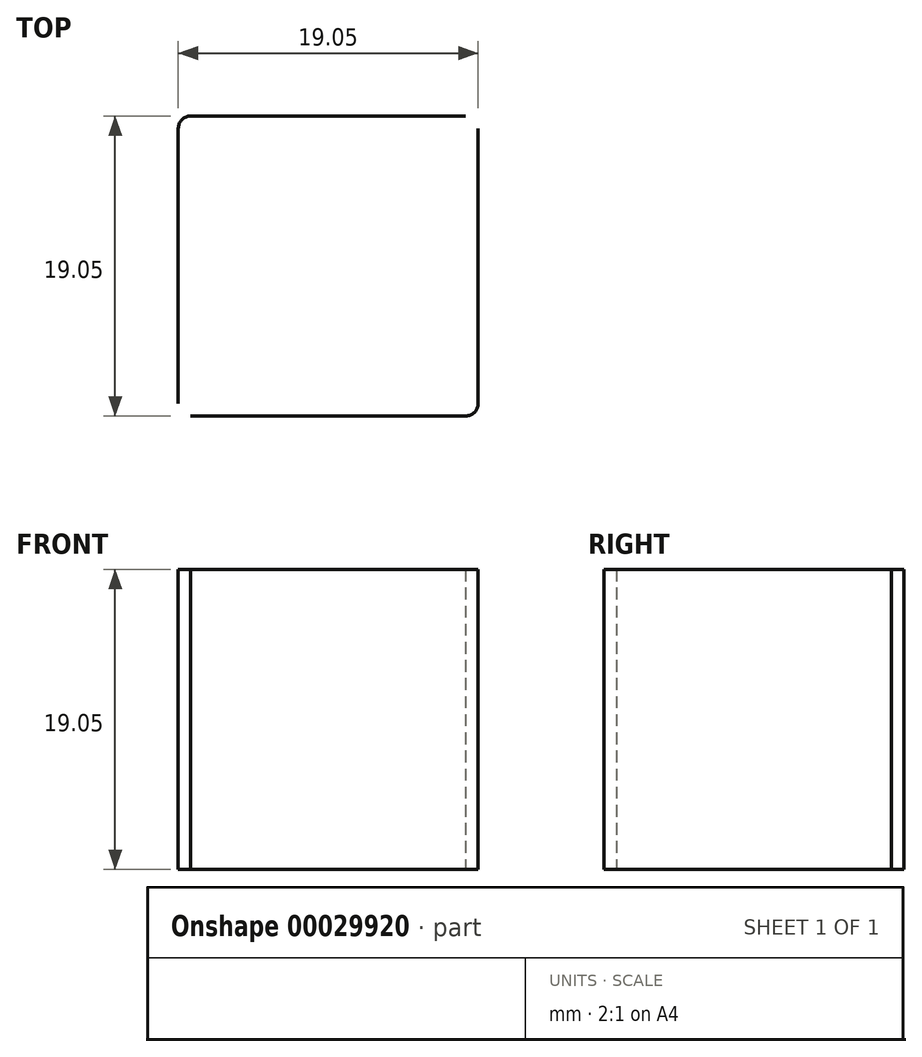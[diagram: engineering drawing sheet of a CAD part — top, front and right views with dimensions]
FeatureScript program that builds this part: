
annotation { "Feature Type Name" : "Feature", "Feature Type Description" : "" }
export const myFeature = defineFeature(function(context is Context, id is Id, definition is map)
    precondition{}
    {
        {
            var Q0;
            Q0=qCreatedBy(makeId("Top.planeOp"),FACE);
            var sketch = newSketch(context, id + "F0", { "sketchPlane" : qUnion([Q0])});
            skLineSegment(sketch, "E0.bottom", {"start": v(-34.1, 33.67) * mm, "end": v(-16.64, 33.67) * mm});
            skLineSegment(sketch, "E0.top", {"start": v(-34.1, -23.48) * mm, "end": v(-16.64, -23.48) * mm});
            skLineSegment(sketch, "E0.left", {"start": v(-34.9, 32.88) * mm, "end": v(-34.9, 15.42) * mm});
            skLineSegment(sketch, "E0.right", {"start": v(22.25, 32.88) * mm, "end": v(22.25, 15.42) * mm});
            skLineSegment(sketch, "E1", {"start": v(-34.9, -22.68) * mm, "end": v(-34.9, -5.22) * mm});
            skLineSegment(sketch, "E2", {"start": v(-34.1, -4.43) * mm, "end": v(-16.64, -4.43) * mm});
            skLineSegment(sketch, "E3", {"start": v(-15.85, -22.68) * mm, "end": v(-15.85, -5.22) * mm});
            skLineSegment(sketch, "E4.0", {"start": v(-34.1, 14.62) * mm, "end": v(-16.64, 14.62) * mm});
            skLineSegment(sketch, "E5.0", {"start": v(3.2, -22.68) * mm, "end": v(3.2, -5.22) * mm});
            skLineSegment(sketch, "E6.bottom", {"start": v(-33.23, -5.2) * mm, "end": v(-17.36, -5.2) * mm});
            skLineSegment(sketch, "E6.top", {"start": v(-33.23, -22.66) * mm, "end": v(-17.36, -22.66) * mm});
            skLineSegment(sketch, "E6.left", {"start": v(-34.03, -6) * mm, "end": v(-34.03, -21.87) * mm});
            skLineSegment(sketch, "E6.right", {"start": v(-16.56, -6) * mm, "end": v(-16.56, -21.87) * mm});
            skPoint(sketch, "E7.visualSharp", {"position": v(-34.03, -5.2) * mm});
            skArc(sketch, "E7.filletArc", {"start": v(-33.23, -5.2) * mm, "mid": v(-33.8, -5.43) * mm, "end": v(-34.03, -6) * mm});
            skPoint(sketch, "E8.visualSharp", {"position": v(-16.56, -5.2) * mm});
            skArc(sketch, "E8.filletArc", {"start": v(-16.56, -6) * mm, "mid": v(-16.8, -5.43) * mm, "end": v(-17.36, -5.2) * mm});
            skPoint(sketch, "E9.visualSharp", {"position": v(-16.56, -22.66) * mm});
            skArc(sketch, "E9.filletArc", {"start": v(-17.36, -22.66) * mm, "mid": v(-16.8, -22.43) * mm, "end": v(-16.56, -21.87) * mm});
            skPoint(sketch, "E10.visualSharp", {"position": v(-34.03, -22.66) * mm});
            skArc(sketch, "E10.filletArc", {"start": v(-34.03, -21.87) * mm, "mid": v(-33.8, -22.43) * mm, "end": v(-33.23, -22.66) * mm});
            skLineSegment(sketch, "E11.0.1.0", {"start": v(-34.03, 13.06) * mm, "end": v(-34.03, -2.82) * mm});
            skArc(sketch, "E11.0.1.1", {"start": v(-34.03, -2.82) * mm, "mid": v(-33.8, -3.38) * mm, "end": v(-33.23, -3.61) * mm});
            skLineSegment(sketch, "E11.0.1.2", {"start": v(-33.23, -3.61) * mm, "end": v(-17.36, -3.61) * mm});
            skArc(sketch, "E11.0.1.3", {"start": v(-17.36, -3.61) * mm, "mid": v(-16.8, -3.38) * mm, "end": v(-16.56, -2.82) * mm});
            skLineSegment(sketch, "E11.0.1.4", {"start": v(-16.56, 13.06) * mm, "end": v(-16.56, -2.82) * mm});
            skArc(sketch, "E11.0.1.5", {"start": v(-16.56, 13.06) * mm, "mid": v(-16.8, 13.62) * mm, "end": v(-17.36, 13.85) * mm});
            skLineSegment(sketch, "E11.0.1.6", {"start": v(-33.23, 13.85) * mm, "end": v(-17.36, 13.85) * mm});
            skArc(sketch, "E11.0.1.7", {"start": v(-33.23, 13.85) * mm, "mid": v(-33.8, 13.62) * mm, "end": v(-34.03, 13.06) * mm});
            skLineSegment(sketch, "E11.0.2.0", {"start": v(-34.03, 32.1) * mm, "end": v(-34.03, 16.23) * mm});
            skArc(sketch, "E11.0.2.1", {"start": v(-34.03, 16.23) * mm, "mid": v(-33.8, 15.67) * mm, "end": v(-33.23, 15.44) * mm});
            skLineSegment(sketch, "E11.0.2.2", {"start": v(-33.23, 15.44) * mm, "end": v(-17.36, 15.44) * mm});
            skArc(sketch, "E11.0.2.3", {"start": v(-17.36, 15.44) * mm, "mid": v(-16.8, 15.67) * mm, "end": v(-16.56, 16.23) * mm});
            skLineSegment(sketch, "E11.0.2.4", {"start": v(-16.56, 32.1) * mm, "end": v(-16.56, 16.23) * mm});
            skArc(sketch, "E11.0.2.5", {"start": v(-16.56, 32.1) * mm, "mid": v(-16.8, 32.67) * mm, "end": v(-17.36, 32.9) * mm});
            skLineSegment(sketch, "E11.0.2.6", {"start": v(-33.23, 32.9) * mm, "end": v(-17.36, 32.9) * mm});
            skArc(sketch, "E11.0.2.7", {"start": v(-33.23, 32.9) * mm, "mid": v(-33.8, 32.67) * mm, "end": v(-34.03, 32.1) * mm});
            skLineSegment(sketch, "E11.1.0.0", {"start": v(-14.98, -6) * mm, "end": v(-14.98, -21.87) * mm});
            skArc(sketch, "E11.1.0.1", {"start": v(-14.98, -21.87) * mm, "mid": v(-14.74, -22.43) * mm, "end": v(-14.18, -22.66) * mm});
            skLineSegment(sketch, "E11.1.0.2", {"start": v(-14.18, -22.66) * mm, "end": v(1.7, -22.66) * mm});
            skArc(sketch, "E11.1.0.3", {"start": v(1.7, -22.66) * mm, "mid": v(2.25, -22.43) * mm, "end": v(2.49, -21.87) * mm});
            skLineSegment(sketch, "E11.1.0.4", {"start": v(2.49, -6) * mm, "end": v(2.49, -21.87) * mm});
            skArc(sketch, "E11.1.0.5", {"start": v(2.49, -6) * mm, "mid": v(2.25, -5.43) * mm, "end": v(1.7, -5.2) * mm});
            skLineSegment(sketch, "E11.1.0.6", {"start": v(-14.18, -5.2) * mm, "end": v(1.7, -5.2) * mm});
            skArc(sketch, "E11.1.0.7", {"start": v(-14.18, -5.2) * mm, "mid": v(-14.74, -5.43) * mm, "end": v(-14.98, -6) * mm});
            skLineSegment(sketch, "E11.1.1.0", {"start": v(-14.98, 13.06) * mm, "end": v(-14.98, -2.82) * mm});
            skArc(sketch, "E11.1.1.1", {"start": v(-14.98, -2.82) * mm, "mid": v(-14.74, -3.38) * mm, "end": v(-14.18, -3.61) * mm});
            skLineSegment(sketch, "E11.1.1.2", {"start": v(-14.18, -3.61) * mm, "end": v(1.7, -3.61) * mm});
            skArc(sketch, "E11.1.1.3", {"start": v(1.7, -3.61) * mm, "mid": v(2.25, -3.38) * mm, "end": v(2.49, -2.82) * mm});
            skLineSegment(sketch, "E11.1.1.4", {"start": v(2.49, 13.06) * mm, "end": v(2.49, -2.82) * mm});
            skArc(sketch, "E11.1.1.5", {"start": v(2.49, 13.06) * mm, "mid": v(2.25, 13.62) * mm, "end": v(1.7, 13.85) * mm});
            skLineSegment(sketch, "E11.1.1.6", {"start": v(-14.18, 13.85) * mm, "end": v(1.7, 13.85) * mm});
            skArc(sketch, "E11.1.1.7", {"start": v(-14.18, 13.85) * mm, "mid": v(-14.74, 13.62) * mm, "end": v(-14.98, 13.06) * mm});
            skLineSegment(sketch, "E11.1.2.0", {"start": v(-14.98, 32.1) * mm, "end": v(-14.98, 16.23) * mm});
            skArc(sketch, "E11.1.2.1", {"start": v(-14.98, 16.23) * mm, "mid": v(-14.74, 15.67) * mm, "end": v(-14.18, 15.44) * mm});
            skLineSegment(sketch, "E11.1.2.2", {"start": v(-14.18, 15.44) * mm, "end": v(1.7, 15.44) * mm});
            skArc(sketch, "E11.1.2.3", {"start": v(1.7, 15.44) * mm, "mid": v(2.25, 15.67) * mm, "end": v(2.49, 16.23) * mm});
            skLineSegment(sketch, "E11.1.2.4", {"start": v(2.49, 32.1) * mm, "end": v(2.49, 16.23) * mm});
            skArc(sketch, "E11.1.2.5", {"start": v(2.49, 32.1) * mm, "mid": v(2.25, 32.67) * mm, "end": v(1.7, 32.9) * mm});
            skLineSegment(sketch, "E11.1.2.6", {"start": v(-14.18, 32.9) * mm, "end": v(1.7, 32.9) * mm});
            skArc(sketch, "E11.1.2.7", {"start": v(-14.18, 32.9) * mm, "mid": v(-14.74, 32.67) * mm, "end": v(-14.98, 32.1) * mm});
            skLineSegment(sketch, "E11.2.0.0", {"start": v(4.07, -6) * mm, "end": v(4.07, -21.87) * mm});
            skArc(sketch, "E11.2.0.1", {"start": v(4.07, -21.87) * mm, "mid": v(4.3, -22.43) * mm, "end": v(4.87, -22.66) * mm});
            skLineSegment(sketch, "E11.2.0.2", {"start": v(4.87, -22.66) * mm, "end": v(20.74, -22.66) * mm});
            skArc(sketch, "E11.2.0.3", {"start": v(20.74, -22.66) * mm, "mid": v(21.3, -22.43) * mm, "end": v(21.54, -21.87) * mm});
            skLineSegment(sketch, "E11.2.0.4", {"start": v(21.54, -6) * mm, "end": v(21.54, -21.87) * mm});
            skArc(sketch, "E11.2.0.5", {"start": v(21.54, -6) * mm, "mid": v(21.3, -5.43) * mm, "end": v(20.74, -5.2) * mm});
            skLineSegment(sketch, "E11.2.0.6", {"start": v(4.87, -5.2) * mm, "end": v(20.74, -5.2) * mm});
            skArc(sketch, "E11.2.0.7", {"start": v(4.87, -5.2) * mm, "mid": v(4.3, -5.43) * mm, "end": v(4.07, -6) * mm});
            skLineSegment(sketch, "E11.2.1.0", {"start": v(4.07, 13.06) * mm, "end": v(4.07, -2.82) * mm});
            skArc(sketch, "E11.2.1.1", {"start": v(4.07, -2.82) * mm, "mid": v(4.3, -3.38) * mm, "end": v(4.87, -3.61) * mm});
            skLineSegment(sketch, "E11.2.1.2", {"start": v(4.87, -3.61) * mm, "end": v(20.74, -3.61) * mm});
            skArc(sketch, "E11.2.1.3", {"start": v(20.74, -3.61) * mm, "mid": v(21.3, -3.38) * mm, "end": v(21.54, -2.82) * mm});
            skLineSegment(sketch, "E11.2.1.4", {"start": v(21.54, 13.06) * mm, "end": v(21.54, -2.82) * mm});
            skArc(sketch, "E11.2.1.5", {"start": v(21.54, 13.06) * mm, "mid": v(21.3, 13.62) * mm, "end": v(20.74, 13.85) * mm});
            skLineSegment(sketch, "E11.2.1.6", {"start": v(4.87, 13.85) * mm, "end": v(20.74, 13.85) * mm});
            skArc(sketch, "E11.2.1.7", {"start": v(4.87, 13.85) * mm, "mid": v(4.3, 13.62) * mm, "end": v(4.07, 13.06) * mm});
            skLineSegment(sketch, "E11.2.2.0", {"start": v(4.07, 32.1) * mm, "end": v(4.07, 16.23) * mm});
            skArc(sketch, "E11.2.2.1", {"start": v(4.07, 16.23) * mm, "mid": v(4.3, 15.67) * mm, "end": v(4.87, 15.44) * mm});
            skLineSegment(sketch, "E11.2.2.2", {"start": v(4.87, 15.44) * mm, "end": v(20.74, 15.44) * mm});
            skArc(sketch, "E11.2.2.3", {"start": v(20.74, 15.44) * mm, "mid": v(21.3, 15.67) * mm, "end": v(21.54, 16.23) * mm});
            skLineSegment(sketch, "E11.2.2.4", {"start": v(21.54, 32.1) * mm, "end": v(21.54, 16.23) * mm});
            skArc(sketch, "E11.2.2.5", {"start": v(21.54, 32.1) * mm, "mid": v(21.3, 32.67) * mm, "end": v(20.74, 32.9) * mm});
            skLineSegment(sketch, "E11.2.2.6", {"start": v(4.87, 32.9) * mm, "end": v(20.74, 32.9) * mm});
            skArc(sketch, "E11.2.2.7", {"start": v(4.87, 32.9) * mm, "mid": v(4.3, 32.67) * mm, "end": v(4.07, 32.1) * mm});
            skLineSegment(sketch, "E12", {"start": v(3.2, 15.42) * mm, "end": v(3.2, 32.88) * mm});
            skLineSegment(sketch, "E13", {"start": v(3.2, -3.63) * mm, "end": v(3.2, 13.83) * mm});
            skLineSegment(sketch, "E14", {"start": v(4, -4.43) * mm, "end": v(21.46, -4.43) * mm});
            skLineSegment(sketch, "E15", {"start": v(4, 14.62) * mm, "end": v(21.46, 14.62) * mm});
            skLineSegment(sketch, "E16", {"start": v(-15.05, 14.62) * mm, "end": v(2.41, 14.62) * mm});
            skLineSegment(sketch, "E17", {"start": v(-15.05, -4.43) * mm, "end": v(2.41, -4.43) * mm});
            skLineSegment(sketch, "E18", {"start": v(-15.85, -3.63) * mm, "end": v(-15.85, 13.83) * mm});
            skLineSegment(sketch, "E19", {"start": v(-15.85, 15.42) * mm, "end": v(-15.85, 32.88) * mm});
            skLineSegment(sketch, "E20", {"start": v(22.25, 13.83) * mm, "end": v(22.25, -3.63) * mm});
            skLineSegment(sketch, "E21", {"start": v(22.25, -5.22) * mm, "end": v(22.25, -22.68) * mm});
            skLineSegment(sketch, "E22", {"start": v(4, -23.48) * mm, "end": v(21.46, -23.48) * mm});
            skLineSegment(sketch, "E23", {"start": v(-15.05, -23.48) * mm, "end": v(2.41, -23.48) * mm});
            skLineSegment(sketch, "E24", {"start": v(-34.9, -5.22) * mm, "end": v(-34.9, -22.68) * mm});
            skLineSegment(sketch, "E25", {"start": v(-34.9, 13.83) * mm, "end": v(-34.9, -3.63) * mm});
            skLineSegment(sketch, "E26", {"start": v(4, 33.67) * mm, "end": v(21.46, 33.67) * mm});
            skLineSegment(sketch, "E27", {"start": v(-15.05, 33.67) * mm, "end": v(2.41, 33.67) * mm});
            skArc(sketch, "E28.filletArc", {"start": v(3.2, 15.42) * mm, "mid": v(3.44, 14.86) * mm, "end": v(4, 14.62) * mm});
            skArc(sketch, "E29.filletArc", {"start": v(21.46, 14.62) * mm, "mid": v(22.02, 14.86) * mm, "end": v(22.25, 15.42) * mm});
            skArc(sketch, "E30.filletArc", {"start": v(4, 33.67) * mm, "mid": v(3.44, 33.44) * mm, "end": v(3.2, 32.88) * mm});
            skArc(sketch, "E31.filletArc", {"start": v(22.25, 32.88) * mm, "mid": v(22.02, 33.44) * mm, "end": v(21.46, 33.67) * mm});
            skArc(sketch, "E32.filletArc", {"start": v(21.46, -4.43) * mm, "mid": v(22.02, -4.2) * mm, "end": v(22.25, -3.63) * mm});
            skArc(sketch, "E33.filletArc", {"start": v(3.2, -3.63) * mm, "mid": v(3.44, -4.2) * mm, "end": v(4, -4.43) * mm});
            skArc(sketch, "E34.filletArc", {"start": v(21.46, -23.48) * mm, "mid": v(22.02, -23.24) * mm, "end": v(22.25, -22.68) * mm});
            skArc(sketch, "E35.filletArc", {"start": v(3.2, -22.68) * mm, "mid": v(3.44, -23.24) * mm, "end": v(4, -23.48) * mm});
            skArc(sketch, "E36.filletArc", {"start": v(-34.1, 33.67) * mm, "mid": v(-34.66, 33.44) * mm, "end": v(-34.9, 32.88) * mm});
            skArc(sketch, "E37.filletArc", {"start": v(-15.85, 32.88) * mm, "mid": v(-16.08, 33.44) * mm, "end": v(-16.64, 33.67) * mm});
            skArc(sketch, "E38.filletArc", {"start": v(-15.05, 14.62) * mm, "mid": v(-15.61, 14.4) * mm, "end": v(-15.85, 13.83) * mm});
            skArc(sketch, "E39.filletArc", {"start": v(-16.64, 14.62) * mm, "mid": v(-16.08, 14.86) * mm, "end": v(-15.85, 15.42) * mm});
            skArc(sketch, "E40.filletArc", {"start": v(-34.9, 15.42) * mm, "mid": v(-34.66, 14.86) * mm, "end": v(-34.1, 14.62) * mm});
            skArc(sketch, "E41.filletArc", {"start": v(-15.85, -5.22) * mm, "mid": v(-16.08, -4.66) * mm, "end": v(-16.64, -4.43) * mm});
            skArc(sketch, "E42.filletArc", {"start": v(-15.85, -3.63) * mm, "mid": v(-15.61, -4.2) * mm, "end": v(-15.05, -4.43) * mm});
            skArc(sketch, "E43.filletArc", {"start": v(-15.85, -22.68) * mm, "mid": v(-15.61, -23.24) * mm, "end": v(-15.05, -23.48) * mm});
            skArc(sketch, "E44.filletArc", {"start": v(-34.1, -4.43) * mm, "mid": v(-34.66, -4.66) * mm, "end": v(-34.9, -5.22) * mm});
            skArc(sketch, "E45.filletArc", {"start": v(-34.9, -22.68) * mm, "mid": v(-34.66, -23.24) * mm, "end": v(-34.1, -23.48) * mm});
            skArc(sketch, "E46.filletArc", {"start": v(22.25, 13.83) * mm, "mid": v(22.02, 14.4) * mm, "end": v(21.46, 14.62) * mm});
            skArc(sketch, "E47.filletArc", {"start": v(4, 14.62) * mm, "mid": v(3.44, 14.4) * mm, "end": v(3.2, 13.83) * mm});
            skLineSegment(sketch, "E48", {"start": v(3.2, 13.83) * mm, "end": v(3.2, -3.63) * mm});
            skArc(sketch, "E49.filletArc", {"start": v(2.41, -4.43) * mm, "mid": v(2.97, -4.2) * mm, "end": v(3.2, -3.63) * mm});
            skArc(sketch, "E50.filletArc", {"start": v(-15.05, -4.43) * mm, "mid": v(-15.61, -4.66) * mm, "end": v(-15.85, -5.22) * mm});
            skArc(sketch, "E51.filletArc", {"start": v(-16.64, -23.48) * mm, "mid": v(-16.08, -23.24) * mm, "end": v(-15.85, -22.68) * mm});
            skLineSegment(sketch, "E52", {"start": v(-15.85, 13.83) * mm, "end": v(-15.85, -3.63) * mm});
            skLineSegment(sketch, "E53", {"start": v(-16.64, -4.43) * mm, "end": v(-34.1, -4.43) * mm});
            skLineSegment(sketch, "E54", {"start": v(-15.85, 32.88) * mm, "end": v(-15.85, 15.42) * mm});
            skArc(sketch, "E55.filletArc", {"start": v(-16.64, -4.43) * mm, "mid": v(-16.08, -4.2) * mm, "end": v(-15.85, -3.63) * mm});
            skArc(sketch, "E56.filletArc", {"start": v(3.2, -5.22) * mm, "mid": v(2.97, -4.66) * mm, "end": v(2.41, -4.43) * mm});
            skArc(sketch, "E57.filletArc", {"start": v(2.41, -23.48) * mm, "mid": v(2.97, -23.24) * mm, "end": v(3.2, -22.68) * mm});
            skArc(sketch, "E58.filletArc", {"start": v(-15.85, 13.83) * mm, "mid": v(-16.08, 14.4) * mm, "end": v(-16.64, 14.62) * mm});
            skArc(sketch, "E59.filletArc", {"start": v(-15.85, 15.42) * mm, "mid": v(-15.61, 14.86) * mm, "end": v(-15.05, 14.62) * mm});
            skArc(sketch, "E60.filletArc", {"start": v(-34.1, 14.62) * mm, "mid": v(-34.66, 14.4) * mm, "end": v(-34.9, 13.83) * mm});
            skArc(sketch, "E61.filletArc", {"start": v(3.2, 13.83) * mm, "mid": v(2.97, 14.4) * mm, "end": v(2.41, 14.62) * mm});
            skArc(sketch, "E62.filletArc", {"start": v(2.41, 14.62) * mm, "mid": v(2.97, 14.86) * mm, "end": v(3.2, 15.42) * mm});
            skArc(sketch, "E63.filletArc", {"start": v(-15.05, 33.67) * mm, "mid": v(-15.61, 33.44) * mm, "end": v(-15.85, 32.88) * mm});
            skArc(sketch, "E64.filletArc", {"start": v(3.2, 32.88) * mm, "mid": v(2.97, 33.44) * mm, "end": v(2.41, 33.67) * mm});
            skArc(sketch, "E65.filletArc", {"start": v(22.25, -5.22) * mm, "mid": v(22.02, -4.66) * mm, "end": v(21.46, -4.43) * mm});
            skArc(sketch, "E66.filletArc", {"start": v(-34.9, -3.63) * mm, "mid": v(-34.66, -4.2) * mm, "end": v(-34.1, -4.43) * mm});
            skArc(sketch, "E67.filletArc", {"start": v(4, -4.43) * mm, "mid": v(3.44, -4.66) * mm, "end": v(3.2, -5.22) * mm});
            skSolve(sketch);
        }
        {
            var Q0;
            Q0=sQuery(id+"F0.wireOp",EDGE,"E26");
            var Q1;
            Q1=sQuery(id+"F0.wireOp",EDGE,"E30.filletArc");
            var Q2;
            Q2=sQuery(id+"F0.wireOp",EDGE,"E12");
            var Q3;
            Q3=sQuery(id+"F0.wireOp",EDGE,"E29.filletArc");
            var Q4;
            Q4=sQuery(id+"F0.wireOp",EDGE,"E0.right");
            var Q5;
            Q5=sQuery(id+"F0.wireOp",EDGE,"E15");
            extrude(context, id + "F1", {"bodyType" : ToolBodyType.SURFACE, "operationType" : NewBodyOperationType.ADD, "surfaceEntities" : qUnion([Q0, Q1, Q2, Q3, Q4, Q5]), "oppositeDirection" : true, "depth" : 19.05 * mm});
        }
    });
